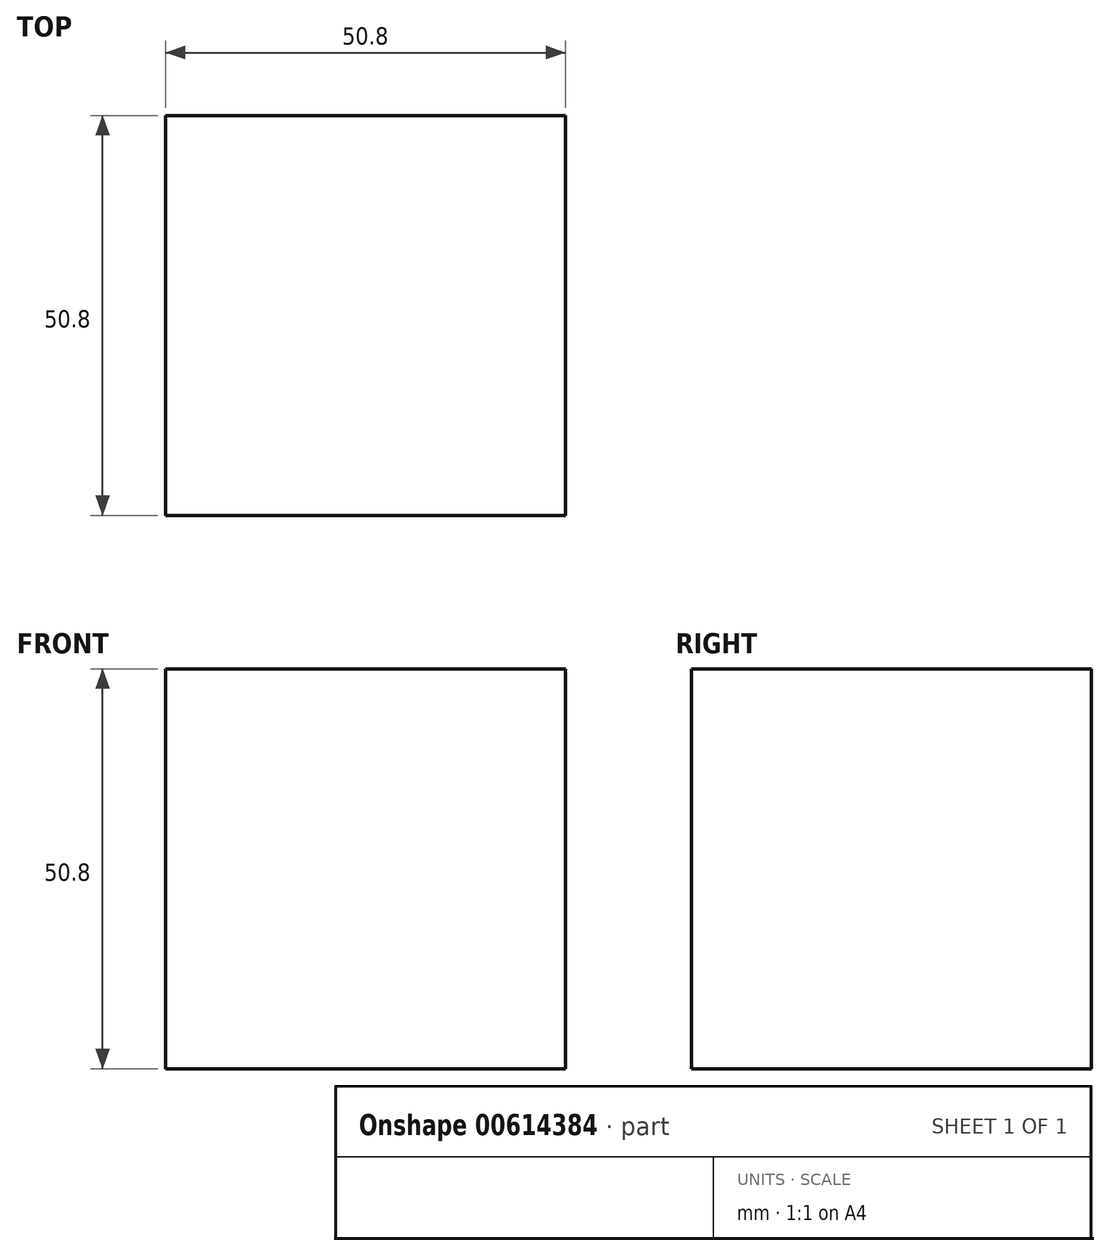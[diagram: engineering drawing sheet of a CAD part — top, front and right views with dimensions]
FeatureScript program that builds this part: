
annotation { "Feature Type Name" : "Feature", "Feature Type Description" : "" }
export const myFeature = defineFeature(function(context is Context, id is Id, definition is map)
    precondition{}
    {
        {
            var Q0;
            Q0=qCreatedBy(makeId("Top.planeOp"),FACE);
            var sketch = newSketch(context, id + "F0", { "sketchPlane" : qUnion([Q0])});
            skLineSegment(sketch, "E0.bottom", {"start": v(-33.27, 46.16) * mm, "end": v(17.53, 46.16) * mm});
            skLineSegment(sketch, "E0.top", {"start": v(-33.27, -4.64) * mm, "end": v(17.53, -4.64) * mm});
            skLineSegment(sketch, "E0.left", {"start": v(-33.27, 46.16) * mm, "end": v(-33.27, -4.64) * mm});
            skLineSegment(sketch, "E0.right", {"start": v(17.53, 46.16) * mm, "end": v(17.53, -4.64) * mm});
            skLineSegment(sketch, "E1", {"start": v(-7.87, 46.16) * mm, "end": v(-33.27, 20.76) * mm});
            skSolve(sketch);
        }
        {
            var Q0;
            {var subQ2=sQuery(id+"F0.wireOp",EDGE,"E0.top");Q0=makeQuery(id+"F0.imprint","IMPRINT",FACE,{"disambiguationData":[TD([[makeQuery(id+"F0.imprint","IMPRINT",EDGE,{"derivedFrom":subQ2}),1.0]])]});}
            var Q1;
            {var subQ3=sQuery(id+"F0.wireOp",EDGE,"E1");Q1=makeQuery(id+"F0.imprint","IMPRINT",FACE,{"disambiguationData":[TD([[makeQuery(id+"F0.imprint","IMPRINT",EDGE,{"derivedFrom":subQ3}),-1.0]])]});}
            extrude(context, id + "F1", {"entities" : qUnion([Q0, Q1]), "depth" : 50.8 * mm, "offsetDistance" : 25.4 * mm});
        }
    });
